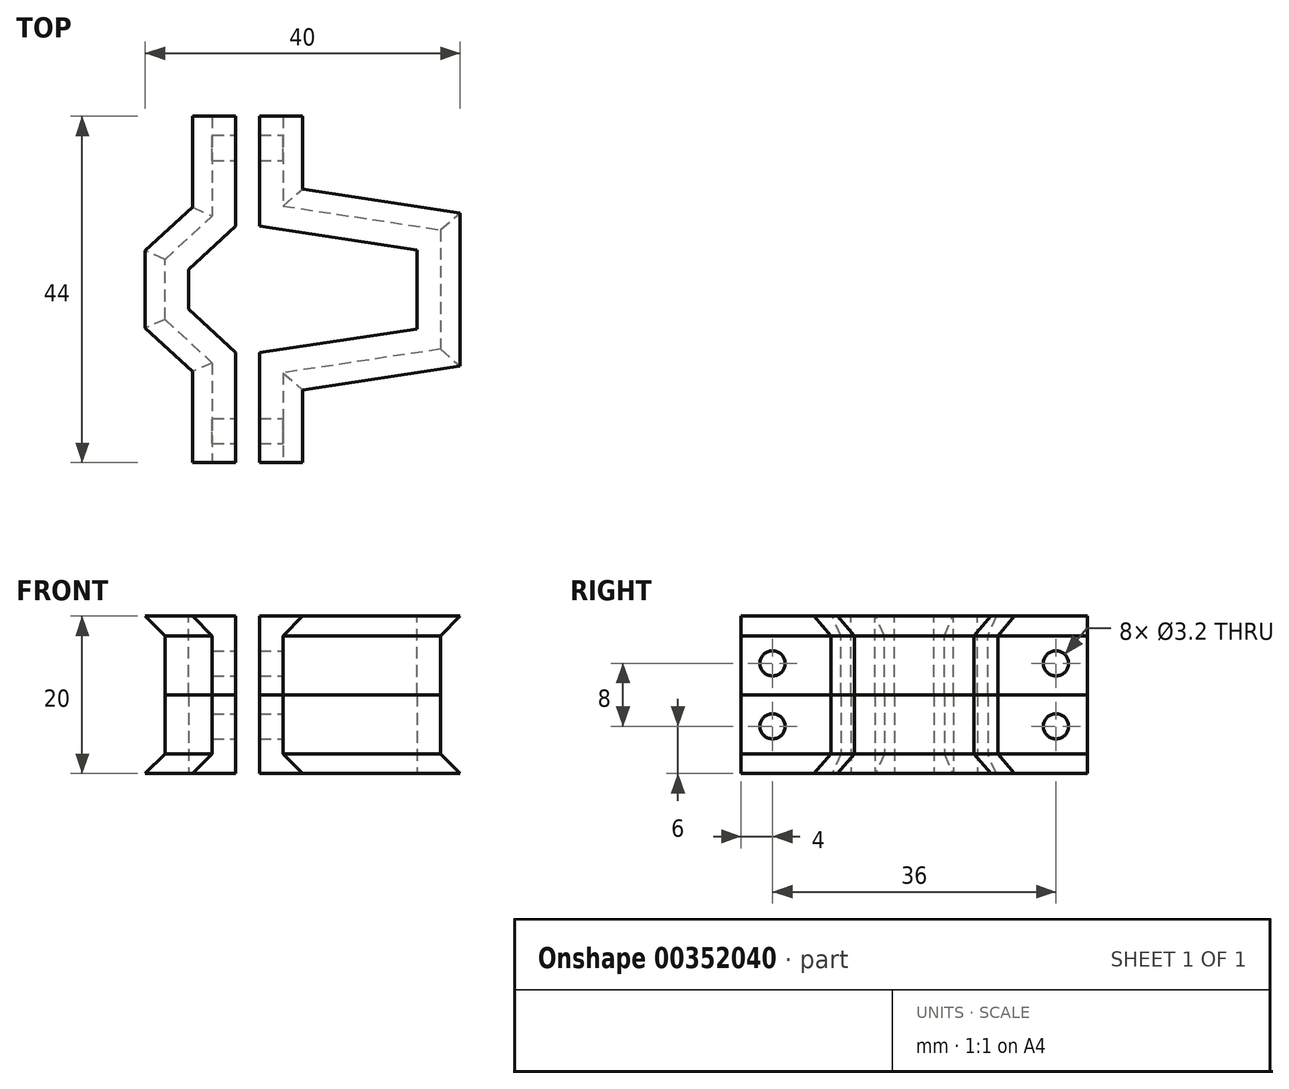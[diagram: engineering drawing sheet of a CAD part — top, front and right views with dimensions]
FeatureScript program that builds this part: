
annotation { "Feature Type Name" : "Feature", "Feature Type Description" : "" }
export const myFeature = defineFeature(function(context is Context, id is Id, definition is map)
    precondition{}
    {
        {
            var Q0;
            Q0=qCreatedBy(makeId("Top.planeOp"),FACE);
            var sketch = newSketch(context, id + "F0", { "sketchPlane" : qUnion([Q0])});
            skLineSegment(sketch, "E0", {"start": v(0, -22) * mm, "end": v(0, -8.02) * mm});
            skLineSegment(sketch, "E1", {"start": v(0, 8.02) * mm, "end": v(0, 22) * mm});
            skLineSegment(sketch, "E2", {"start": v(0, -22) * mm, "end": v(-3, -22) * mm});
            skLineSegment(sketch, "E3", {"start": v(0, 22) * mm, "end": v(-3, 22) * mm});
            skLineSegment(sketch, "E4", {"start": v(-3, 22) * mm, "end": v(-3, 9.34) * mm});
            skLineSegment(sketch, "E5", {"start": v(0, -8.02) * mm, "end": v(-6, -2.5) * mm});
            skLineSegment(sketch, "E6", {"start": v(-6, 2.5) * mm, "end": v(0, 8.02) * mm});
            skLineSegment(sketch, "E7", {"start": v(-6, -2.5) * mm, "end": v(-6, 2.5) * mm});
            skPoint(sketch, "E8.orphan", {"position": v(-8.72, 0) * mm});
            skLineSegment(sketch, "E9", {"start": v(-9, 3.82) * mm, "end": v(-3, 9.34) * mm});
            skLineSegment(sketch, "E10", {"start": v(-9, -3.82) * mm, "end": v(-9, 0) * mm});
            skLineSegment(sketch, "E11", {"start": v(-9, 0) * mm, "end": v(-9, 3.82) * mm});
            skLineSegment(sketch, "E12.trimOffspring", {"start": v(-3, -9.34) * mm, "end": v(-3, -22) * mm});
            skLineSegment(sketch, "E13", {"start": v(-9, -3.82) * mm, "end": v(-3, -9.34) * mm});
            skLineSegment(sketch, "E14", {"start": v(0, 8.02) * mm, "end": v(0, 0) * mm, "construction": true});
            skLineSegment(sketch, "E15", {"start": v(0, 0) * mm, "end": v(0, -8.02) * mm, "construction": true});
            skSolve(sketch);
        }
        {
            var Q0;
            Q0 = qSketchRegion(id + "F0", true);
            extrude(context, id + "F1", {"entities" : qUnion([Q0]), "depth" : 10 * mm});
        }
        {
            var Q0;
            Q0=makeQuery(id+"F1.opExtrude","SWEPT_FACE",FACE,{"disambiguationData":[OSD([sQuery(id+"F0.wireOp",EDGE,"E0")])]});
            var sketch = newSketch(context, id + "F2", { "sketchPlane" : qUnion([Q0])});
            skCircle(sketch, "E16", {"center": v(-18, 6) * mm, "radius": 1.6 * mm});
            skCircle(sketch, "E17", {"center": v(18, 6) * mm, "radius": 1.6 * mm});
            skLineSegment(sketch, "E18", {"start": v(-18, 6) * mm, "end": v(0, 6) * mm, "construction": true});
            skLineSegment(sketch, "E19", {"start": v(0, 6) * mm, "end": v(18, 6) * mm, "construction": true});
            skSolve(sketch);
        }
        {
            var Q0;
            Q0 = qSketchRegion(id + "F2", true);
            extrude(context, id + "F3", {"entities" : qUnion([Q0]), "operationType" : NewBodyOperationType.REMOVE, "endBound" : BoundingType.UP_TO_NEXT, "oppositeDirection" : true, "depth" : 25 * mm});
        }
        {
            var Q0;
            Q0=qCreatedBy(makeId("Top.planeOp"),FACE);
            var sketch = newSketch(context, id + "F4", { "sketchPlane" : qUnion([Q0])});
            skLineSegment(sketch, "E20", {"start": v(3, -22) * mm, "end": v(3, -8.02) * mm});
            skLineSegment(sketch, "E21", {"start": v(3, -8.02) * mm, "end": v(23, -5) * mm});
            skLineSegment(sketch, "E22", {"start": v(23, -5) * mm, "end": v(23, 0) * mm});
            skLineSegment(sketch, "E23", {"start": v(23, 0) * mm, "end": v(23, 5) * mm});
            skLineSegment(sketch, "E24", {"start": v(23, 5) * mm, "end": v(3, 8.02) * mm});
            skLineSegment(sketch, "E25", {"start": v(3, 8.02) * mm, "end": v(3, 22) * mm});
            skLineSegment(sketch, "E26", {"start": v(3, 22) * mm, "end": v(6, 22) * mm});
            skLineSegment(sketch, "E27", {"start": v(6, 22) * mm, "end": v(6, 10.6) * mm});
            skLineSegment(sketch, "E28", {"start": v(6, 10.6) * mm, "end": v(26, 7.58) * mm});
            skLineSegment(sketch, "E29", {"start": v(26, 7.58) * mm, "end": v(26, -7.58) * mm});
            skLineSegment(sketch, "E30", {"start": v(26, -7.58) * mm, "end": v(6, -10.6) * mm});
            skLineSegment(sketch, "E31", {"start": v(6, -10.6) * mm, "end": v(6, -22) * mm});
            skLineSegment(sketch, "E32", {"start": v(6, -22) * mm, "end": v(3, -22) * mm});
            skSolve(sketch);
        }
        {
            var Q0;
            Q0 = qSketchRegion(id + "F4", true);
            extrude(context, id + "F5", {"entities" : qUnion([Q0]), "depth" : 10 * mm});
        }
        {
            var Q0;
            Q0=makeQuery(id+"F5.opExtrude","SWEPT_FACE",FACE,{"disambiguationData":[OSD([sQuery(id+"F4.wireOp",EDGE,"E31")])]});
            var sketch = newSketch(context, id + "F6", { "sketchPlane" : qUnion([Q0])});
            skCircle(sketch, "E33", {"center": v(-18, 6) * mm, "radius": 1.6 * mm});
            skCircle(sketch, "E34", {"center": v(18, 6) * mm, "radius": 1.6 * mm});
            skLineSegment(sketch, "E35", {"start": v(-18, 6) * mm, "end": v(0, 6) * mm, "construction": true});
            skLineSegment(sketch, "E36", {"start": v(0, 6) * mm, "end": v(18, 6) * mm, "construction": true});
            skSolve(sketch);
        }
        {
            var Q0;
            Q0 = qSketchRegion(id + "F6", true);
            extrude(context, id + "F7", {"entities" : qUnion([Q0]), "operationType" : NewBodyOperationType.REMOVE, "endBound" : BoundingType.UP_TO_NEXT, "oppositeDirection" : true, "depth" : 25 * mm});
        }
        {
            var Q0;
            Q0=makeQuery(id+"F1.opExtrude","CAP_FACE",FACE,{"disambiguationData":[OSD([sQuery(id+"F0.wireOp",EDGE,"E0"),sQuery(id+"F0.wireOp",EDGE,"E1"),sQuery(id+"F0.wireOp",EDGE,"E2"),sQuery(id+"F0.wireOp",EDGE,"E3"),sQuery(id+"F0.wireOp",EDGE,"E4"),sQuery(id+"F0.wireOp",EDGE,"E5"),sQuery(id+"F0.wireOp",EDGE,"E6"),sQuery(id+"F0.wireOp",EDGE,"E7"),sQuery(id+"F0.wireOp",EDGE,"E9"),sQuery(id+"F0.wireOp",EDGE,"E10"),sQuery(id+"F0.wireOp",EDGE,"E11"),sQuery(id+"F0.wireOp",EDGE,"E12.trimOffspring"),sQuery(id+"F0.wireOp",EDGE,"E13")])],"isStart":true});
            var sketch = newSketch(context, id + "F8", { "sketchPlane" : qUnion([Q0])});
            skLineSegment(sketch, "E37", {"start": v(-3, 22) * mm, "end": v(-3, 9.34) * mm});
            skLineSegment(sketch, "E38", {"start": v(-3, 9.34) * mm, "end": v(-9, 3.82) * mm});
            skLineSegment(sketch, "E39", {"start": v(-9, 3.82) * mm, "end": v(-9, -3.82) * mm});
            skLineSegment(sketch, "E40", {"start": v(-9, -3.82) * mm, "end": v(-3, -9.34) * mm});
            skLineSegment(sketch, "E41", {"start": v(-3, -9.34) * mm, "end": v(-3, -22) * mm});
            skLineSegment(sketch, "E42", {"start": v(-3, -22) * mm, "end": v(-5.5, -22) * mm});
            skLineSegment(sketch, "E43", {"start": v(-5.5, -22) * mm, "end": v(-5.5, -10.43) * mm});
            skLineSegment(sketch, "E44", {"start": v(-5.5, -10.43) * mm, "end": v(-11.5, -4.91) * mm});
            skLineSegment(sketch, "E45", {"start": v(-11.5, -4.91) * mm, "end": v(-11.5, 4.91) * mm});
            skLineSegment(sketch, "E46", {"start": v(-11.5, 4.91) * mm, "end": v(-5.5, 10.43) * mm});
            skLineSegment(sketch, "E47", {"start": v(-5.5, 10.43) * mm, "end": v(-5.5, 22) * mm});
            skLineSegment(sketch, "E48", {"start": v(-5.5, 22) * mm, "end": v(-3, 22) * mm});
            skSolve(sketch);
        }
        {
            var Q0;
            Q0 = qSketchRegion(id + "F8", true);
            extrude(context, id + "F9", {"entities" : qUnion([Q0]), "operationType" : NewBodyOperationType.ADD, "oppositeDirection" : true, "depth" : 2.5 * mm});
        }
        {
            var Q0;
            Q0=makeQuery(id+"F5.opExtrude","CAP_FACE",FACE,{"disambiguationData":[OSD([sQuery(id+"F4.wireOp",EDGE,"E20"),sQuery(id+"F4.wireOp",EDGE,"E21"),sQuery(id+"F4.wireOp",EDGE,"E22"),sQuery(id+"F4.wireOp",EDGE,"E23"),sQuery(id+"F4.wireOp",EDGE,"E24"),sQuery(id+"F4.wireOp",EDGE,"E25"),sQuery(id+"F4.wireOp",EDGE,"E26"),sQuery(id+"F4.wireOp",EDGE,"E27"),sQuery(id+"F4.wireOp",EDGE,"E28"),sQuery(id+"F4.wireOp",EDGE,"E29"),sQuery(id+"F4.wireOp",EDGE,"E30"),sQuery(id+"F4.wireOp",EDGE,"E31"),sQuery(id+"F4.wireOp",EDGE,"E32")])],"isStart":true});
            var sketch = newSketch(context, id + "F10", { "sketchPlane" : qUnion([Q0])});
            skLineSegment(sketch, "E49", {"start": v(6, -22) * mm, "end": v(8.5, -22) * mm});
            skLineSegment(sketch, "E50", {"start": v(8.5, -22) * mm, "end": v(8.5, -12.75) * mm});
            skLineSegment(sketch, "E51", {"start": v(8.5, -12.75) * mm, "end": v(28.5, -9.73) * mm});
            skLineSegment(sketch, "E52", {"start": v(28.5, -9.73) * mm, "end": v(28.5, 9.73) * mm});
            skLineSegment(sketch, "E53", {"start": v(28.5, 9.73) * mm, "end": v(8.5, 12.75) * mm});
            skLineSegment(sketch, "E54", {"start": v(8.5, 12.75) * mm, "end": v(8.5, 22) * mm});
            skLineSegment(sketch, "E55", {"start": v(8.5, 22) * mm, "end": v(6, 22) * mm});
            skLineSegment(sketch, "E56", {"start": v(6, 22) * mm, "end": v(6, 10.6) * mm});
            skLineSegment(sketch, "E57", {"start": v(6, 10.6) * mm, "end": v(26, 7.58) * mm});
            skLineSegment(sketch, "E58", {"start": v(26, 7.58) * mm, "end": v(26, -7.58) * mm});
            skLineSegment(sketch, "E59", {"start": v(26, -7.58) * mm, "end": v(6, -10.6) * mm});
            skLineSegment(sketch, "E60", {"start": v(6, -10.6) * mm, "end": v(6, -22) * mm});
            skSolve(sketch);
        }
        {
            var Q0;
            Q0 = qSketchRegion(id + "F10", true);
            extrude(context, id + "F11", {"entities" : qUnion([Q0]), "operationType" : NewBodyOperationType.ADD, "oppositeDirection" : true, "depth" : 2.5 * mm});
        }
        {
            var Q0;
            Q0=makeQuery(id+"F11.opExtrude","CAP_EDGE",EDGE,{"disambiguationData":[OSD([sQuery(id+"F10.wireOp",EDGE,"E50")])],"isStart":false});
            var Q1;
            Q1=makeQuery(id+"F11.opExtrude","CAP_EDGE",EDGE,{"disambiguationData":[OSD([sQuery(id+"F10.wireOp",EDGE,"E51")])],"isStart":false});
            var Q2;
            Q2=makeQuery(id+"F11.opExtrude","CAP_EDGE",EDGE,{"disambiguationData":[OSD([sQuery(id+"F10.wireOp",EDGE,"E52")])],"isStart":false});
            var Q3;
            Q3=makeQuery(id+"F11.opExtrude","CAP_EDGE",EDGE,{"disambiguationData":[OSD([sQuery(id+"F10.wireOp",EDGE,"E53")])],"isStart":false});
            var Q4;
            Q4=makeQuery(id+"F11.opExtrude","CAP_EDGE",EDGE,{"disambiguationData":[OSD([sQuery(id+"F10.wireOp",EDGE,"E54")])],"isStart":false});
            var Q5;
            Q5=makeQuery(id+"F9.opExtrude","CAP_EDGE",EDGE,{"disambiguationData":[OSD([sQuery(id+"F8.wireOp",EDGE,"E43")])],"isStart":false});
            var Q6;
            Q6=makeQuery(id+"F9.opExtrude","CAP_EDGE",EDGE,{"disambiguationData":[OSD([sQuery(id+"F8.wireOp",EDGE,"E44")])],"isStart":false});
            var Q7;
            Q7=makeQuery(id+"F9.opExtrude","CAP_EDGE",EDGE,{"disambiguationData":[OSD([sQuery(id+"F8.wireOp",EDGE,"E45")])],"isStart":false});
            var Q8;
            Q8=makeQuery(id+"F9.opExtrude","CAP_EDGE",EDGE,{"disambiguationData":[OSD([sQuery(id+"F8.wireOp",EDGE,"E46")])],"isStart":false});
            var Q9;
            Q9=makeQuery(id+"F9.opExtrude","CAP_EDGE",EDGE,{"disambiguationData":[OSD([sQuery(id+"F8.wireOp",EDGE,"E47")])],"isStart":false});
            chamfer(context, id + "F12", {"entities" : qUnion([Q0, Q1, Q2, Q3, Q4, Q5, Q6, Q7, Q8, Q9]), "width" : 2.5 * mm, "tangentPropagation" : true});
        }
        {
            var Q0;
            Q0=makeQuery(id+"F1.opExtrude","SWEPT_BODY",BODY,{"disambiguationData":[OSD([sQuery(id+"F0.wireOp",EDGE,"E0"),sQuery(id+"F0.wireOp",EDGE,"E1"),sQuery(id+"F0.wireOp",EDGE,"E2"),sQuery(id+"F0.wireOp",EDGE,"E3"),sQuery(id+"F0.wireOp",EDGE,"E4"),sQuery(id+"F0.wireOp",EDGE,"E5"),sQuery(id+"F0.wireOp",EDGE,"E6"),sQuery(id+"F0.wireOp",EDGE,"E7"),sQuery(id+"F0.wireOp",EDGE,"E9"),sQuery(id+"F0.wireOp",EDGE,"E10"),sQuery(id+"F0.wireOp",EDGE,"E11"),sQuery(id+"F0.wireOp",EDGE,"E12.trimOffspring"),sQuery(id+"F0.wireOp",EDGE,"E13")])]});
            var Q1;
            Q1=makeQuery(id+"F5.opExtrude","SWEPT_BODY",BODY,{"disambiguationData":[OSD([sQuery(id+"F4.wireOp",EDGE,"E20"),sQuery(id+"F4.wireOp",EDGE,"E21"),sQuery(id+"F4.wireOp",EDGE,"E22"),sQuery(id+"F4.wireOp",EDGE,"E23"),sQuery(id+"F4.wireOp",EDGE,"E24"),sQuery(id+"F4.wireOp",EDGE,"E25"),sQuery(id+"F4.wireOp",EDGE,"E26"),sQuery(id+"F4.wireOp",EDGE,"E27"),sQuery(id+"F4.wireOp",EDGE,"E28"),sQuery(id+"F4.wireOp",EDGE,"E29"),sQuery(id+"F4.wireOp",EDGE,"E30"),sQuery(id+"F4.wireOp",EDGE,"E31"),sQuery(id+"F4.wireOp",EDGE,"E32")])]});
            var Q2;
            Q2=makeQuery(id+"F1.opExtrude","CAP_FACE",FACE,{"disambiguationData":[OSD([sQuery(id+"F0.wireOp",EDGE,"E0"),sQuery(id+"F0.wireOp",EDGE,"E1"),sQuery(id+"F0.wireOp",EDGE,"E2"),sQuery(id+"F0.wireOp",EDGE,"E3"),sQuery(id+"F0.wireOp",EDGE,"E4"),sQuery(id+"F0.wireOp",EDGE,"E5"),sQuery(id+"F0.wireOp",EDGE,"E6"),sQuery(id+"F0.wireOp",EDGE,"E7"),sQuery(id+"F0.wireOp",EDGE,"E9"),sQuery(id+"F0.wireOp",EDGE,"E10"),sQuery(id+"F0.wireOp",EDGE,"E11"),sQuery(id+"F0.wireOp",EDGE,"E12.trimOffspring"),sQuery(id+"F0.wireOp",EDGE,"E13")])],"isStart":false});
            mirror(context, id + "F13", {"entities" : qUnion([Q0, Q1]), "mirrorPlane" : qUnion([Q2])});
        }
    });
